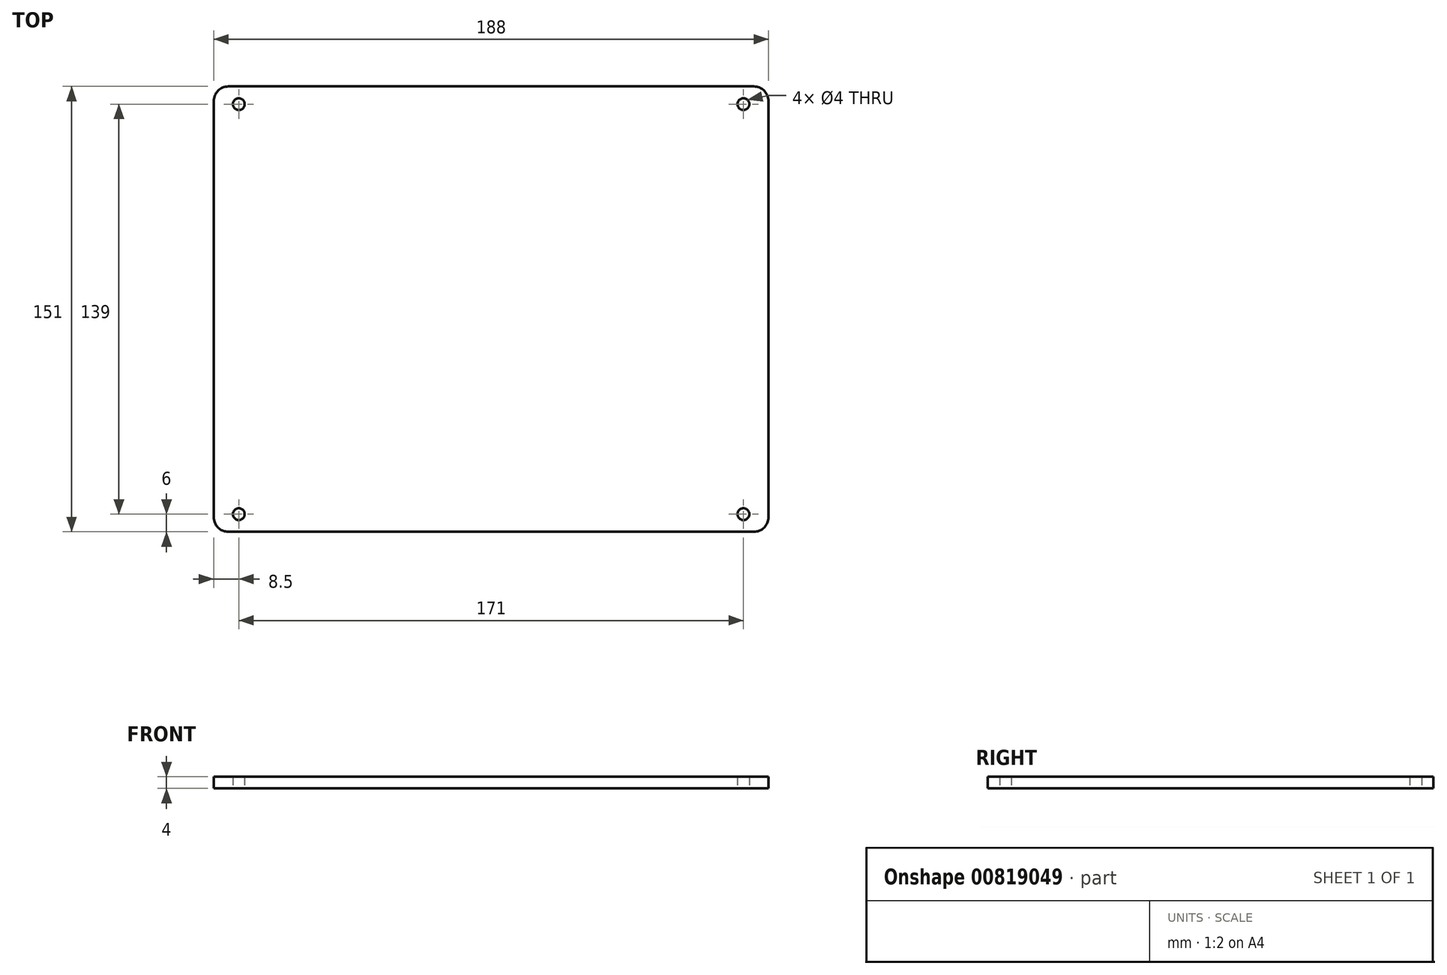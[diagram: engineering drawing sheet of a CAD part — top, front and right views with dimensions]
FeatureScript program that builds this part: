
annotation { "Feature Type Name" : "Feature", "Feature Type Description" : "" }
export const myFeature = defineFeature(function(context is Context, id is Id, definition is map)
    precondition{}
    {
        {
            var Q0;
            Q0=qCreatedBy(makeId("Top.planeOp"),FACE);
            var sketch = newSketch(context, id + "F0", { "sketchPlane" : qUnion([Q0])});
            skLineSegment(sketch, "E0.bottom", {"start": v(89, 75.5) * mm, "end": v(-89, 75.5) * mm});
            skLineSegment(sketch, "E0.top", {"start": v(89, -75.5) * mm, "end": v(-89, -75.5) * mm});
            skLineSegment(sketch, "E0.left", {"start": v(94, 70.5) * mm, "end": v(94, -70.5) * mm});
            skLineSegment(sketch, "E0.right", {"start": v(-94, 70.5) * mm, "end": v(-94, -70.5) * mm});
            skPoint(sketch, "E0.middle", {"position": v(0, 0) * mm});
            skPoint(sketch, "E1.visualSharp", {"position": v(-94, 75.5) * mm});
            skArc(sketch, "E1.filletArc", {"start": v(-89, 75.5) * mm, "mid": v(-92.54, 74.04) * mm, "end": v(-94, 70.5) * mm});
            skPoint(sketch, "E2.visualSharp", {"position": v(-94, -75.5) * mm});
            skArc(sketch, "E2.filletArc", {"start": v(-94, -70.5) * mm, "mid": v(-92.54, -74.04) * mm, "end": v(-89, -75.5) * mm});
            skPoint(sketch, "E3.visualSharp", {"position": v(94, -75.5) * mm});
            skArc(sketch, "E3.filletArc", {"start": v(89, -75.5) * mm, "mid": v(92.54, -74.04) * mm, "end": v(94, -70.5) * mm});
            skPoint(sketch, "E4.visualSharp", {"position": v(94, 75.5) * mm});
            skArc(sketch, "E4.filletArc", {"start": v(94, 70.5) * mm, "mid": v(92.54, 74.04) * mm, "end": v(89, 75.5) * mm});
            skLineSegment(sketch, "E5", {"start": v(-94, -69.5) * mm, "end": v(-59.84, -69.5) * mm, "construction": true});
            skLineSegment(sketch, "E6", {"start": v(-85.5, -75.5) * mm, "end": v(-85.5, -52.19) * mm, "construction": true});
            skPoint(sketch, "E7", {"position": v(-85.5, -69.5) * mm});
            skCircle(sketch, "E8", {"center": v(-85.5, -69.5) * mm, "radius": 2 * mm});
            skLineSegment(sketch, "E9", {"start": v(-73.59, 0) * mm, "end": v(72.33, 0) * mm, "construction": true});
            skLineSegment(sketch, "E10", {"start": v(0, -73.29) * mm, "end": v(0, 57.51) * mm, "construction": true});
            skCircle(sketch, "E11.MirrorC", {"center": v(85.5, -69.5) * mm, "radius": 2 * mm});
            skCircle(sketch, "E12.MirrorC", {"center": v(85.5, 69.5) * mm, "radius": 2 * mm});
            skCircle(sketch, "E13.MirrorC", {"center": v(-85.5, 69.5) * mm, "radius": 2 * mm});
            skSolve(sketch);
        }
        {
            var Q0;
            Q0 = qSketchRegion(id + "F0", true);
            extrude(context, id + "F1", {"entities" : qUnion([Q0]), "depth" : 2 * mm, "offsetDistance" : 25 * mm});
        }
        {
            var Q0;
            Q0=makeQuery(id+"F1.opExtrude","CAP_FACE",FACE,{"disambiguationData":[OSD([sQuery(id+"F0.wireOp",EDGE,"E0.bottom"),sQuery(id+"F0.wireOp",EDGE,"E0.top"),sQuery(id+"F0.wireOp",EDGE,"E0.left"),sQuery(id+"F0.wireOp",EDGE,"E0.right"),sQuery(id+"F0.wireOp",EDGE,"E1.filletArc"),sQuery(id+"F0.wireOp",EDGE,"E2.filletArc"),sQuery(id+"F0.wireOp",EDGE,"E3.filletArc"),sQuery(id+"F0.wireOp",EDGE,"E4.filletArc")])],"isStart":false});
            var sketch = newSketch(context, id + "F2", { "sketchPlane" : qUnion([Q0])});
            skLineSegment(sketch, "E14.bottom", {"start": v(89, 75.5) * mm, "end": v(-89, 75.5) * mm});
            skLineSegment(sketch, "E14.top", {"start": v(89, -75.5) * mm, "end": v(-89, -75.5) * mm});
            skLineSegment(sketch, "E14.left", {"start": v(94, 70.5) * mm, "end": v(94, -70.5) * mm});
            skLineSegment(sketch, "E14.right", {"start": v(-94, 70.5) * mm, "end": v(-94, -70.5) * mm});
            skPoint(sketch, "E14.middle", {"position": v(0, 0) * mm});
            skPoint(sketch, "E15.visualSharp", {"position": v(-94, 75.5) * mm});
            skArc(sketch, "E15.filletArc", {"start": v(-89, 75.5) * mm, "mid": v(-92.54, 74.04) * mm, "end": v(-94, 70.5) * mm});
            skPoint(sketch, "E16.visualSharp", {"position": v(-94, -75.5) * mm});
            skArc(sketch, "E16.filletArc", {"start": v(-94, -70.5) * mm, "mid": v(-92.54, -74.04) * mm, "end": v(-89, -75.5) * mm});
            skPoint(sketch, "E17.visualSharp", {"position": v(94, -75.5) * mm});
            skArc(sketch, "E17.filletArc", {"start": v(89, -75.5) * mm, "mid": v(92.54, -74.04) * mm, "end": v(94, -70.5) * mm});
            skPoint(sketch, "E18.visualSharp", {"position": v(94, 75.5) * mm});
            skArc(sketch, "E18.filletArc", {"start": v(94, 70.5) * mm, "mid": v(92.54, 74.04) * mm, "end": v(89, 75.5) * mm});
            skSolve(sketch);
        }
        {
            var Q0;
            Q0 = qSketchRegion(id + "F2", true);
            var Q1;
            Q1 = qSketchRegion(id + "F0", true);
            extrude(context, id + "F3", {"entities" : qUnion([Q0, Q1]), "operationType" : NewBodyOperationType.ADD, "depth" : 2 * mm, "offsetDistance" : 25 * mm});
        }
        {
            var Q0;
            Q0=makeQuery(id+"F3.boolean.opBoolean","SPLIT",FACE,{"disambiguationData":[TD([makeQuery(id+"F1.opExtrude","SWEPT_FACE",FACE,{"disambiguationData":[OSD([sQuery(id+"F0.wireOp",EDGE,"E13.MirrorC")])]})])],"derivedFrom":makeQuery(id+"F3.opExtrude","CAP_FACE",FACE,{"disambiguationData":[OSD([sQuery(id+"F2.wireOp",EDGE,"E14.bottom"),sQuery(id+"F2.wireOp",EDGE,"E14.top"),sQuery(id+"F2.wireOp",EDGE,"E14.left"),sQuery(id+"F2.wireOp",EDGE,"E14.right"),sQuery(id+"F2.wireOp",EDGE,"E15.filletArc"),sQuery(id+"F2.wireOp",EDGE,"E16.filletArc"),sQuery(id+"F2.wireOp",EDGE,"E17.filletArc"),sQuery(id+"F2.wireOp",EDGE,"E18.filletArc")])],"isStart":true})});
            var Q1;
            Q1=makeQuery(id+"F3.boolean.opBoolean","SPLIT",FACE,{"disambiguationData":[TD([makeQuery(id+"F1.opExtrude","SWEPT_FACE",FACE,{"disambiguationData":[OSD([sQuery(id+"F0.wireOp",EDGE,"E12.MirrorC")])]})])],"derivedFrom":makeQuery(id+"F3.opExtrude","CAP_FACE",FACE,{"disambiguationData":[OSD([sQuery(id+"F2.wireOp",EDGE,"E14.bottom"),sQuery(id+"F2.wireOp",EDGE,"E14.top"),sQuery(id+"F2.wireOp",EDGE,"E14.left"),sQuery(id+"F2.wireOp",EDGE,"E14.right"),sQuery(id+"F2.wireOp",EDGE,"E15.filletArc"),sQuery(id+"F2.wireOp",EDGE,"E16.filletArc"),sQuery(id+"F2.wireOp",EDGE,"E17.filletArc"),sQuery(id+"F2.wireOp",EDGE,"E18.filletArc")])],"isStart":true})});
            var Q2;
            Q2=makeQuery(id+"F3.boolean.opBoolean","SPLIT",FACE,{"disambiguationData":[TD([makeQuery(id+"F1.opExtrude","SWEPT_FACE",FACE,{"disambiguationData":[OSD([sQuery(id+"F0.wireOp",EDGE,"E11.MirrorC")])]})])],"derivedFrom":makeQuery(id+"F3.opExtrude","CAP_FACE",FACE,{"disambiguationData":[OSD([sQuery(id+"F2.wireOp",EDGE,"E14.bottom"),sQuery(id+"F2.wireOp",EDGE,"E14.top"),sQuery(id+"F2.wireOp",EDGE,"E14.left"),sQuery(id+"F2.wireOp",EDGE,"E14.right"),sQuery(id+"F2.wireOp",EDGE,"E15.filletArc"),sQuery(id+"F2.wireOp",EDGE,"E16.filletArc"),sQuery(id+"F2.wireOp",EDGE,"E17.filletArc"),sQuery(id+"F2.wireOp",EDGE,"E18.filletArc")])],"isStart":true})});
            var Q3;
            Q3=makeQuery(id+"F3.boolean.opBoolean","SPLIT",FACE,{"disambiguationData":[TD([makeQuery(id+"F1.opExtrude","SWEPT_FACE",FACE,{"disambiguationData":[OSD([sQuery(id+"F0.wireOp",EDGE,"E8")])]})])],"derivedFrom":makeQuery(id+"F3.opExtrude","CAP_FACE",FACE,{"disambiguationData":[OSD([sQuery(id+"F2.wireOp",EDGE,"E14.bottom"),sQuery(id+"F2.wireOp",EDGE,"E14.top"),sQuery(id+"F2.wireOp",EDGE,"E14.left"),sQuery(id+"F2.wireOp",EDGE,"E14.right"),sQuery(id+"F2.wireOp",EDGE,"E15.filletArc"),sQuery(id+"F2.wireOp",EDGE,"E16.filletArc"),sQuery(id+"F2.wireOp",EDGE,"E17.filletArc"),sQuery(id+"F2.wireOp",EDGE,"E18.filletArc")])],"isStart":true})});
            var Q4;
            Q4=sQuery(id+"F0.wireOp",EDGE,"E8");
            var Q5;
            Q5=sQuery(id+"F0.wireOp",EDGE,"E11.MirrorC");
            var Q6;
            Q6=sQuery(id+"F0.wireOp",EDGE,"E12.MirrorC");
            var Q7;
            Q7=sQuery(id+"F0.wireOp",EDGE,"E13.MirrorC");
            extrude(context, id + "F4", {"entities" : qUnion([Q0, Q1, Q2, Q3]), "operationType" : NewBodyOperationType.REMOVE, "surfaceEntities" : qUnion([Q4, Q5, Q6, Q7]), "endBound" : BoundingType.THROUGH_ALL, "oppositeDirection" : true, "depth" : 25 * mm, "offsetDistance" : 25 * mm});
        }
    });
